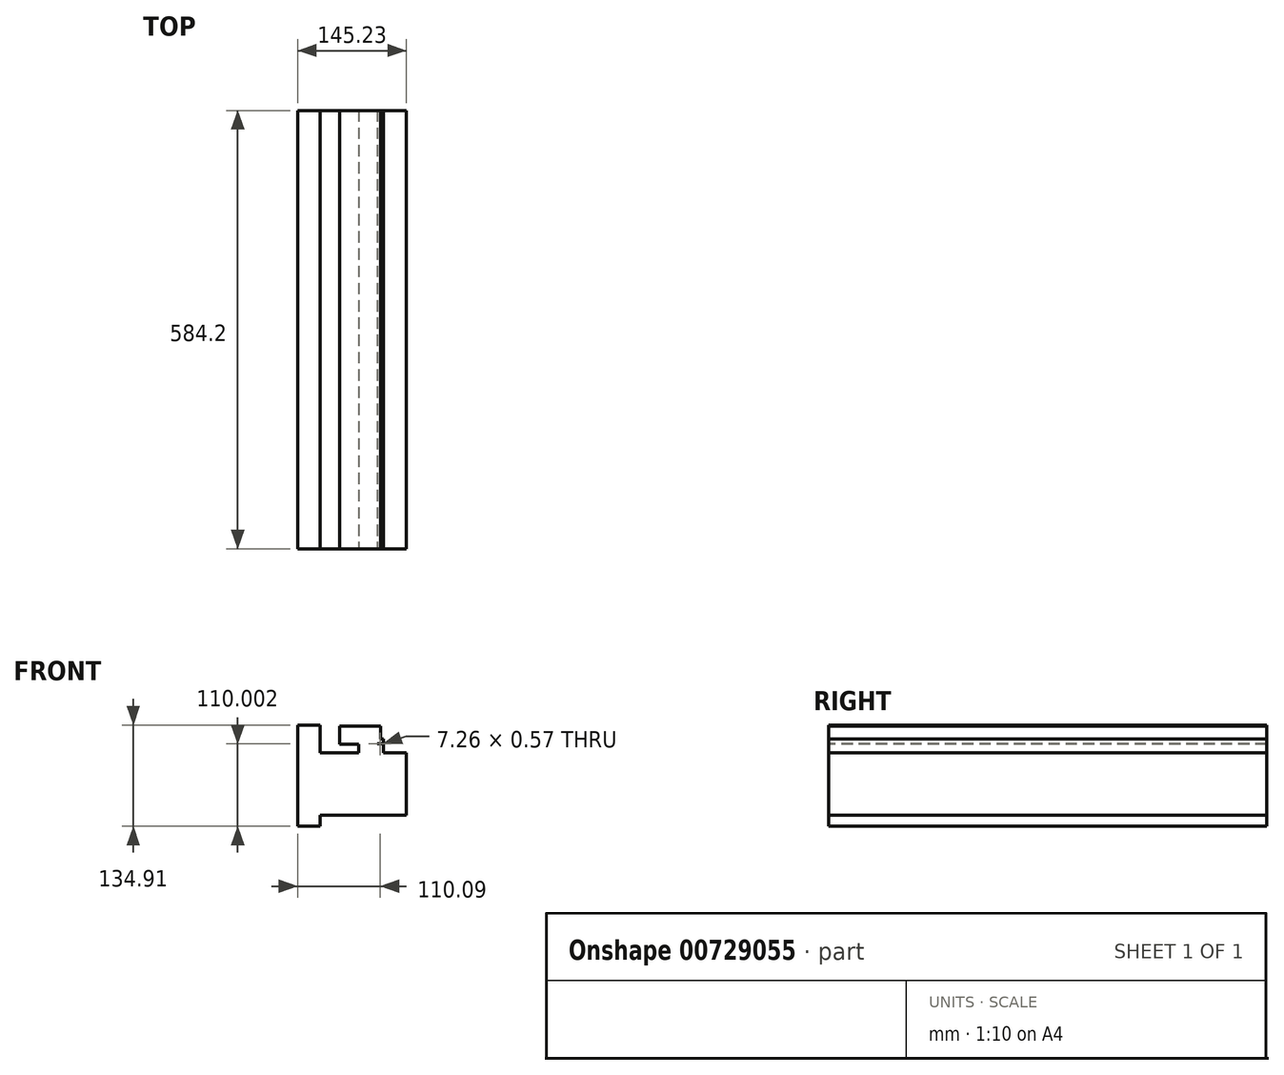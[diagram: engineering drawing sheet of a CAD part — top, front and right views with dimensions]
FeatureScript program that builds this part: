
annotation { "Feature Type Name" : "Feature", "Feature Type Description" : "" }
export const myFeature = defineFeature(function(context is Context, id is Id, definition is map)
    precondition{}
    {
        {
            var Q0;
            Q0=qCreatedBy(makeId("Front.planeOp"),FACE);
            var sketch = newSketch(context, id + "F0", { "sketchPlane" : qUnion([Q0])});
            skLineSegment(sketch, "E0.bottom", {"start": v(24.86, 37.36) * mm, "end": v(32.12, 37.36) * mm});
            skLineSegment(sketch, "E0.top", {"start": v(24.86, 37.93) * mm, "end": v(32.12, 37.93) * mm});
            skLineSegment(sketch, "E0.left", {"start": v(24.86, 37.36) * mm, "end": v(24.86, 37.93) * mm});
            skLineSegment(sketch, "E0.right", {"start": v(32.12, 37.36) * mm, "end": v(32.12, 37.93) * mm});
            skLineSegment(sketch, "E1.bottom", {"start": v(0, 43.72) * mm, "end": v(33, 43.72) * mm});
            skLineSegment(sketch, "E1.top", {"start": v(0, -19.18) * mm, "end": v(33, -19.18) * mm});
            skLineSegment(sketch, "E1.left", {"start": v(0, 43.72) * mm, "end": v(0, -19.18) * mm});
            skLineSegment(sketch, "E1.right", {"start": v(33, 43.72) * mm, "end": v(33, -19.18) * mm});
            skLineSegment(sketch, "E2.bottom", {"start": v(63.63, 25.5) * mm, "end": v(-79.86, 25.5) * mm});
            skLineSegment(sketch, "E2.top", {"start": v(63.63, -57.39) * mm, "end": v(-79.86, -57.39) * mm});
            skLineSegment(sketch, "E2.left", {"start": v(63.63, 25.5) * mm, "end": v(63.63, -57.39) * mm});
            skLineSegment(sketch, "E2.right", {"start": v(-79.86, 25.5) * mm, "end": v(-79.86, -57.39) * mm});
            skLineSegment(sketch, "E3.bottom", {"start": v(-81.6, -72.36) * mm, "end": v(-51.76, -72.36) * mm});
            skLineSegment(sketch, "E3.top", {"start": v(-81.6, 62.55) * mm, "end": v(-51.76, 62.55) * mm});
            skLineSegment(sketch, "E3.left", {"start": v(-81.6, -72.36) * mm, "end": v(-81.6, 62.55) * mm});
            skLineSegment(sketch, "E3.right", {"start": v(-51.76, -72.36) * mm, "end": v(-51.76, 62.55) * mm});
            skLineSegment(sketch, "E4.bottom", {"start": v(29.02, 61.22) * mm, "end": v(-25.27, 61.22) * mm});
            skLineSegment(sketch, "E4.top", {"start": v(29.02, 37.26) * mm, "end": v(-25.27, 37.26) * mm});
            skLineSegment(sketch, "E4.left", {"start": v(29.02, 61.22) * mm, "end": v(29.02, 37.26) * mm});
            skLineSegment(sketch, "E4.right", {"start": v(-25.27, 61.22) * mm, "end": v(-25.27, 37.26) * mm});
            skSolve(sketch);
        }
        {
            var Q0;
            {var subQ0=sQuery(id+"F0.wireOp",EDGE,"E1.top");Q0=makeQuery(id+"F0.imprint","IMPRINT",FACE,{"disambiguationData":[TD([[makeQuery(id+"F0.imprint","IMPRINT",EDGE,{"derivedFrom":subQ0}),1.0]])]});}
            var Q1;
            {var subQ0=sQuery(id+"F0.wireOp",EDGE,"E2.right");Q1=makeQuery(id+"F0.imprint","IMPRINT",FACE,{"disambiguationData":[TD([[makeQuery(id+"F0.imprint","IMPRINT",EDGE,{"derivedFrom":subQ0}),-1.0]])]});}
            var Q2;
            {var subQ9=sQuery(id+"F0.wireOp",EDGE,"E0.right");Q2=makeQuery(id+"F0.imprint","IMPRINT",FACE,{"disambiguationData":[TD([[makeQuery(id+"F0.imprint","IMPRINT",EDGE,{"derivedFrom":subQ9}),-1.0]])]});}
            var Q3;
            {var subQ5=sQuery(id+"F0.wireOp",EDGE,"E1.top");Q3=makeQuery(id+"F0.imprint","IMPRINT",FACE,{"disambiguationData":[TD([[makeQuery(id+"F0.imprint","IMPRINT",EDGE,{"derivedFrom":subQ5}),-1.0]])]});}
            var Q4;
            {var subQ5=sQuery(id+"F0.wireOp",EDGE,"E0.left");Q4=makeQuery(id+"F0.imprint","IMPRINT",FACE,{"disambiguationData":[TD([[makeQuery(id+"F0.imprint","IMPRINT",EDGE,{"derivedFrom":subQ5}),1.0]])]});}
            var Q5;
            {var subQ0=sQuery(id+"F0.wireOp",EDGE,"E2.right");Q5=makeQuery(id+"F0.imprint","IMPRINT",FACE,{"disambiguationData":[TD([[makeQuery(id+"F0.imprint","IMPRINT",EDGE,{"derivedFrom":subQ0}),1.0]])]});}
            var Q6;
            {var subQ4=sQuery(id+"F0.wireOp",EDGE,"E4.bottom");Q6=makeQuery(id+"F0.imprint","IMPRINT",FACE,{"disambiguationData":[TD([[makeQuery(id+"F0.imprint","IMPRINT",EDGE,{"derivedFrom":subQ4}),1.0]])]});}
            extrude(context, id + "F1", {"entities" : qUnion([Q0, Q1, Q2, Q3, Q4, Q5, Q6]), "oppositeDirection" : true, "depth" : 584.2 * mm, "offsetDistance" : 25.4 * mm});
        }
    });
